# Revit family: Door-Sliding-DORMA-ST_FLEX_Green-Double_Panel
name_source: partatom
category: Türen
revit_build: Autodesk Revit Architecture 2016 (Build: 20150220_1215(x64)
units: mm (PartAtom-declared; Revit-internal decimal feet)

## family parameters
Basisbauteil = Wand
Beim Laden mit Abzugskörper schneiden = Nein
Gemeinsam genutzt = Nein
Immer vertikal = Ja
OmniClass-Nummer = 23.30.10.00
OmniClass-Titel = Doors
Raumberechnungspunkt = Nein

## types (1)
- Door-Sliding-DORMA-ST_FLEX_Green-Double_Panel
    Activation = DORMA Prosecure Opti Combi combined radar activation and threshold infrared safety sensor, Hard wired or wireless wall switch actuation satin stainless steel 150 x 150mm (Option), Slimline jamb switch satin stainless steel 115 x 45mm (Option), Link to access control (By others). DORMA require a normally open volt free contact momentarily closed on receipt of a valid signal from the access control system (Option)
    AdmissibleHumidity = max. 93 %
    AdmissibleTemperature = -20 to + 60 °C
    Beschreibung = Energy saving automatic sliding door system ST-FLEX Green
    BusConnection = Protocol DORMA Connect and Work
    Category = Sliding Doors
    ClearPassageHeightMax = 0 mm  [stored 0 ft]
    ClearPassageHeightMin = 0 mm  [stored 0 ft]
    ClearPassageWidthMax = 0 mm  [stored 0 ft]
    ClearPassageWidthMin = 0 mm  [stored 0 ft]
    ClosingSpeed = 10 to 50 cm/s
    CodePerformance = EN 16005, DIN 18650, EnEV 2009, EN ISO 10077, ISO 14025
    Depth (mm) = 0
    Design country = Germany
    DocumentReference = www.dorma.com
    DoorPanelWeightMax = max. 2 x 160 kg
    EPD Certification = http://www.dorma.com
    Edition number = 0
    ElectricalRequirements  = The electrical contractor shall provide a 240-volt AC mains spur to the right-hand side of the opening above and on the same face that each drive unit is fitted. The spur must be switched and fused with a central flex outlet faceplate. A 10 amp residual circuit breaker at the mains board and a 5-amp fuse at the spur shall protect the circuit.
    EmergencyPowerSupply = Rechargeable battery pack (optional)
    EscapeRoute = Nein
    ExpectedLife = 1000000 operation cycles
    FanlightOptions = one-piece, two-part, 3-part version
    FireExit = Nein
    FloorRail = Continuous floor-integrated guide rail. The floor guide rail is always required and has to be provided by others!
    Frame Material = Aluminum 5005
    Glass Material = Glass
    Height (mm) = 0
    Hersteller = DORMA Deutschland GmbH
    HoldOpenTime = 0 to 180 s
    IFC Classification = Door
    IfcExportAs = IfcDoor
    IfcExportType = IfcDoorStyle
    IsAutomaticReversing = Ja
    IsExternal = Ja
    IsoCode = ISO 9001
    Locking = Electromechanical locking device (bistable), Manual lock release for electromechanical locking device, Read-out error log with error codes, Pharmacy Function
    Manufacturer country = Germany
    ManufacturerURL = www.dorma.com
    Material = Metall
    Material main = Metal
    Material secondary = Stell
    ModelLabel = ST-FLEX Green
    ModelReference = ST-FLEX
    NBSDescription = Sliding Doorset Systems
    NBSReference = 25-30-20-77
    Name = Sliding Door System ST-FLEX Green
    OpeningClosingForceMax = 150 N
    OpeningSpeed = 10 to 75 cm/s
    OpeningStyle = Sliding
    OperatorDepth = 0 mm  [stored 0 ft]
    OperatorHeight = 0 mm  [stored 0 ft]
    Options = Parametrisation via PDA, Emergency opening/closing (only with rechargeable battery pack), 24 V output for external accessories, Bell contact
    OutputVoltage = 24 V
    PowerConsumption = 180 to 250 W
    Product certification = http://www.dorma.com
    ProductInformation = www.dorma.com
    Profile system = DORMA Profile System ST FLEX
    ProgrammFunctions = Off,  Automatic, Permanent Open, Partial Open, Exit Only, Night-/Bank Function
    ProtectionClass = IP 20
    Revision = 10
    SafetyDevices = Self-regulating safety system monitoring all door movements including closing force. Auto reverse function if the doors make contact with an obstruction during the closing cycle (infrared threshold safety sensor).
    Sensor = Combined sensors to DIN 18650 and EN 16005
    Shape = Rectangle
    SlidingDoorOperator = DORMA ES 200, ES 200-D (Escape Route)
    Specification Text = http://www.dorma.com
    StructuralTolerance = 0 mm  [stored 0 ft]
    SupplyVolatageFrequence = 50/60 Hz
    SupplyVoltage = 230 V
    Technical Leaflet = http://www.dorma.com
    Technical description = http://www.dorma.com
    ThermalTransmittance = 1.4 to 1.8
    UNPSC name = Elkraftsutrustning och tillbehör
    UNSPC code = 26
    Uniclass2 = SS-25-30-20-77
    Version = 10
    WallRequirements = Masonry to DIN 1053-1: Nominal thickness larger than 115 mm, Mortar group II, Crushing resistance of brickwork larger 12; Steel concrete to DIN 1045:  Nominal thickness larger 100 mm, Strength class B15
    Wandabschluss = Nach Basisbauteil
    Width (mm) = 0

note: [stored X ft] marks values corroborated as IEEE doubles in the binary element streams (Revit-internal decimal feet)

## geometry (parser evidence)
native form markers: Blend x4, Sweep x30
no freeform markers — native parametric forms only
